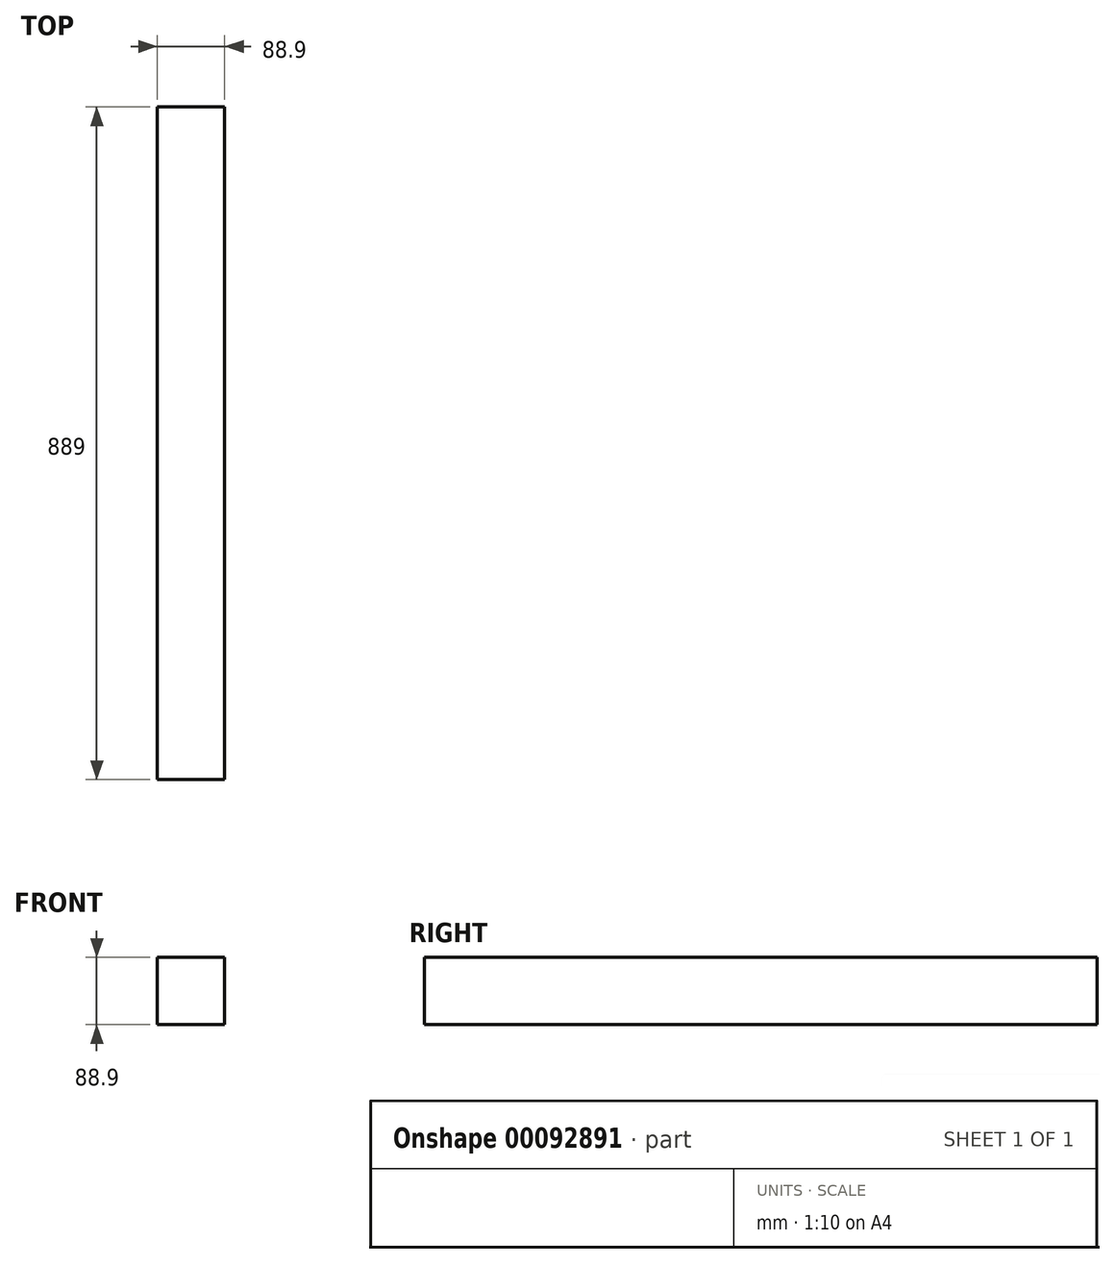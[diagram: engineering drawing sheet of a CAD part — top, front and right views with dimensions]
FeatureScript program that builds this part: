
annotation { "Feature Type Name" : "Feature", "Feature Type Description" : "" }
export const myFeature = defineFeature(function(context is Context, id is Id, definition is map)
    precondition{}
    {
        {
            var Q0;
            Q0=qCreatedBy(makeId("Front.planeOp"),FACE);
            var sketch = newSketch(context, id + "F0", { "sketchPlane" : qUnion([Q0])});
            skLineSegment(sketch, "E0.bottom", {"start": v(-88.9, 88.9) * mm, "end": v(0, 88.9) * mm});
            skLineSegment(sketch, "E0.top", {"start": v(-88.9, 0) * mm, "end": v(0, 0) * mm});
            skLineSegment(sketch, "E0.left", {"start": v(-88.9, 88.9) * mm, "end": v(-88.9, 0) * mm});
            skLineSegment(sketch, "E0.right", {"start": v(0, 88.9) * mm, "end": v(0, 0) * mm});
            skSolve(sketch);
        }
        {
            var Q0;
            Q0 = qSketchRegion(id + "F0", true);
            extrude(context, id + "F1", {"entities" : qUnion([Q0]), "depth" : 889 * mm});
        }
    });
